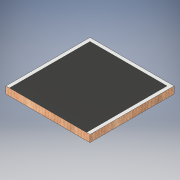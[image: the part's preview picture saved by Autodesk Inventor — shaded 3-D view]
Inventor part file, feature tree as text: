
AUTODESK INVENTOR PART (.ipt)
format: ipt  version: 2017 (Build 210142000, 142)  size: 118,272 bytes
history: native  units: in
note: dims shown in document units (in); Inventor stores cm internally (conversion verified against a paired STEP export)
features: extrude x2, sketch x2
ambient origin geometry x8: Origin, YZ Plane, XZ Plane, XY Plane, X Axis, Y Axis, Z Axis, Center Point
bodies: Solid1 (feature_tree)
feature tree (4):
  extrude  "Extrusion1"  Depth=12.0in
  extrude  "Extrusion2"  Depth=11.0in
  sketch  "Sketch1"  dims[d0=12.0in d1=12.0in]
  sketch  "Sketch2"  dims[d2=11.0in d3=11.0in d4=1.0in d5=0.0in d6=12.0in d7=11.0in d8=11.0in d9=0.0001in d10=0.0in]
